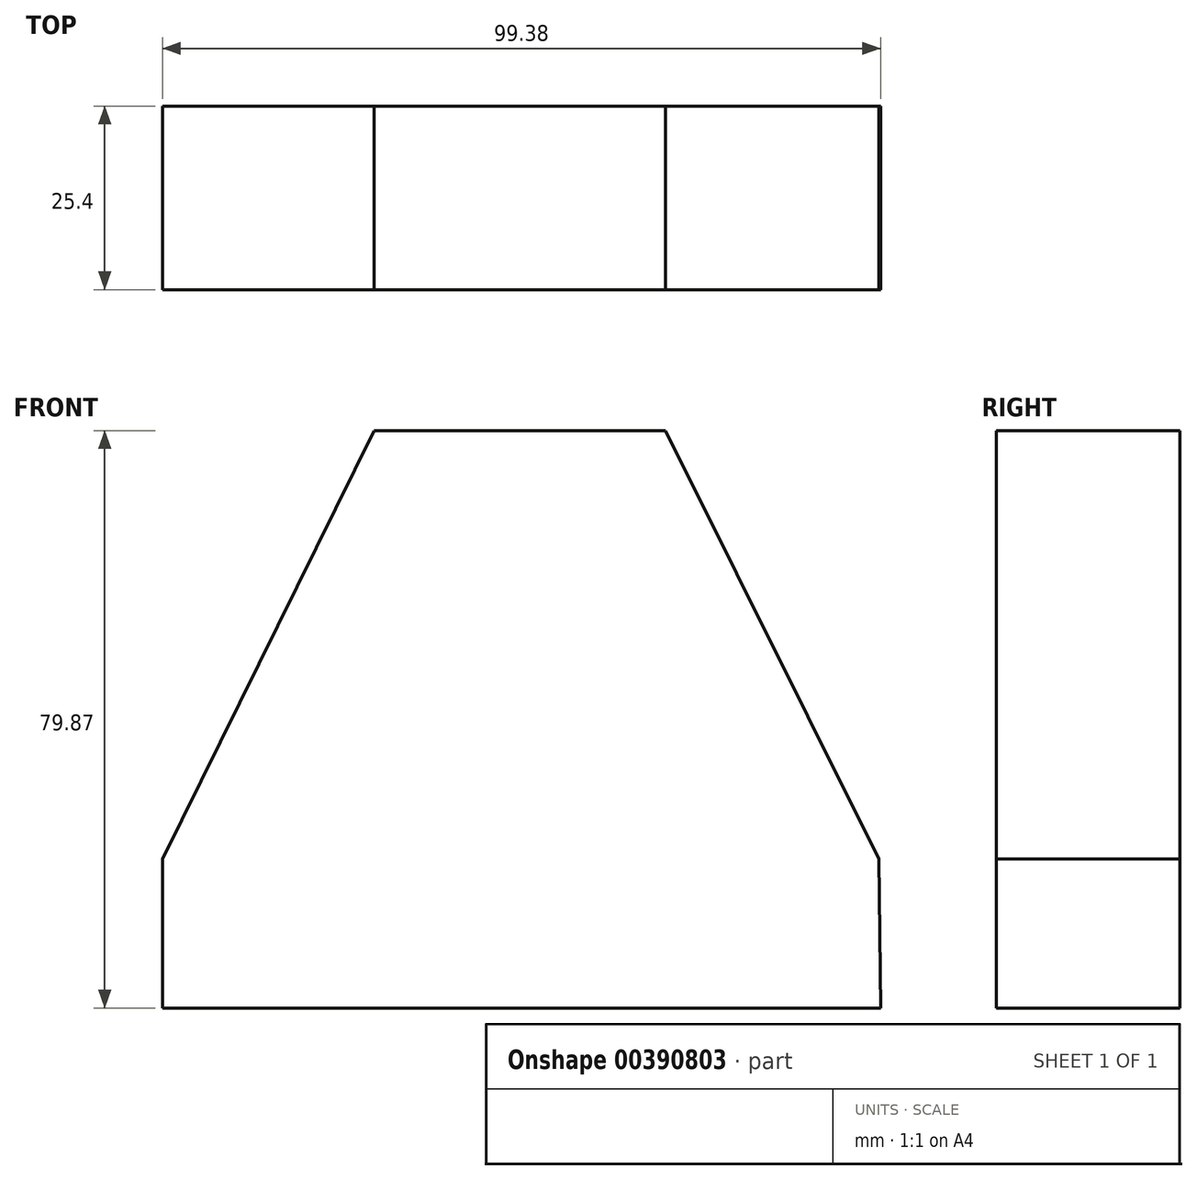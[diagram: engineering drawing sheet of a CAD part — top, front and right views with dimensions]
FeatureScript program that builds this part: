
annotation { "Feature Type Name" : "Feature", "Feature Type Description" : "" }
export const myFeature = defineFeature(function(context is Context, id is Id, definition is map)
    precondition{}
    {
        {
            var Q0;
            Q0=qCreatedBy(makeId("Front.planeOp"),FACE);
            var sketch = newSketch(context, id + "F0", { "sketchPlane" : qUnion([Q0])});
            skLineSegment(sketch, "E0.bottom", {"start": v(-20.72, -36.76) * mm, "end": v(19.6, -36.76) * mm});
            skLineSegment(sketch, "E0.top", {"start": v(-20.72, 43.1) * mm, "end": v(19.6, 43.1) * mm});
            skLineSegment(sketch, "E1", {"start": v(-20.72, 43.1) * mm, "end": v(-50, -16.13) * mm});
            skLineSegment(sketch, "E2", {"start": v(-50, -36.76) * mm, "end": v(49.4, -36.76) * mm});
            skLineSegment(sketch, "E3", {"start": v(49.14, -16.13) * mm, "end": v(19.6, 43.1) * mm});
            skLineSegment(sketch, "E4", {"start": v(-50, -36.76) * mm, "end": v(-50, -16.13) * mm});
            skLineSegment(sketch, "E5", {"start": v(49.14, -16.13) * mm, "end": v(49.4, -36.76) * mm});
            skPoint(sketch, "E6.orphan", {"position": v(-60.18, -36.76) * mm});
            skSolve(sketch);
        }
        {
            var Q0;
            Q0=makeQuery(id+"F0.imprint","IMPRINT",FACE,{"disambiguationData":[TD([[makeQuery(id+"F0.imprint","IMPRINT",EDGE,{"derivedFrom":sQuery(id+"F0.wireOp",EDGE,"E0.top")}),-1.0]])]});
            extrude(context, id + "F1", {"entities" : qUnion([Q0]), "depth" : 25.4 * mm});
        }
    });
